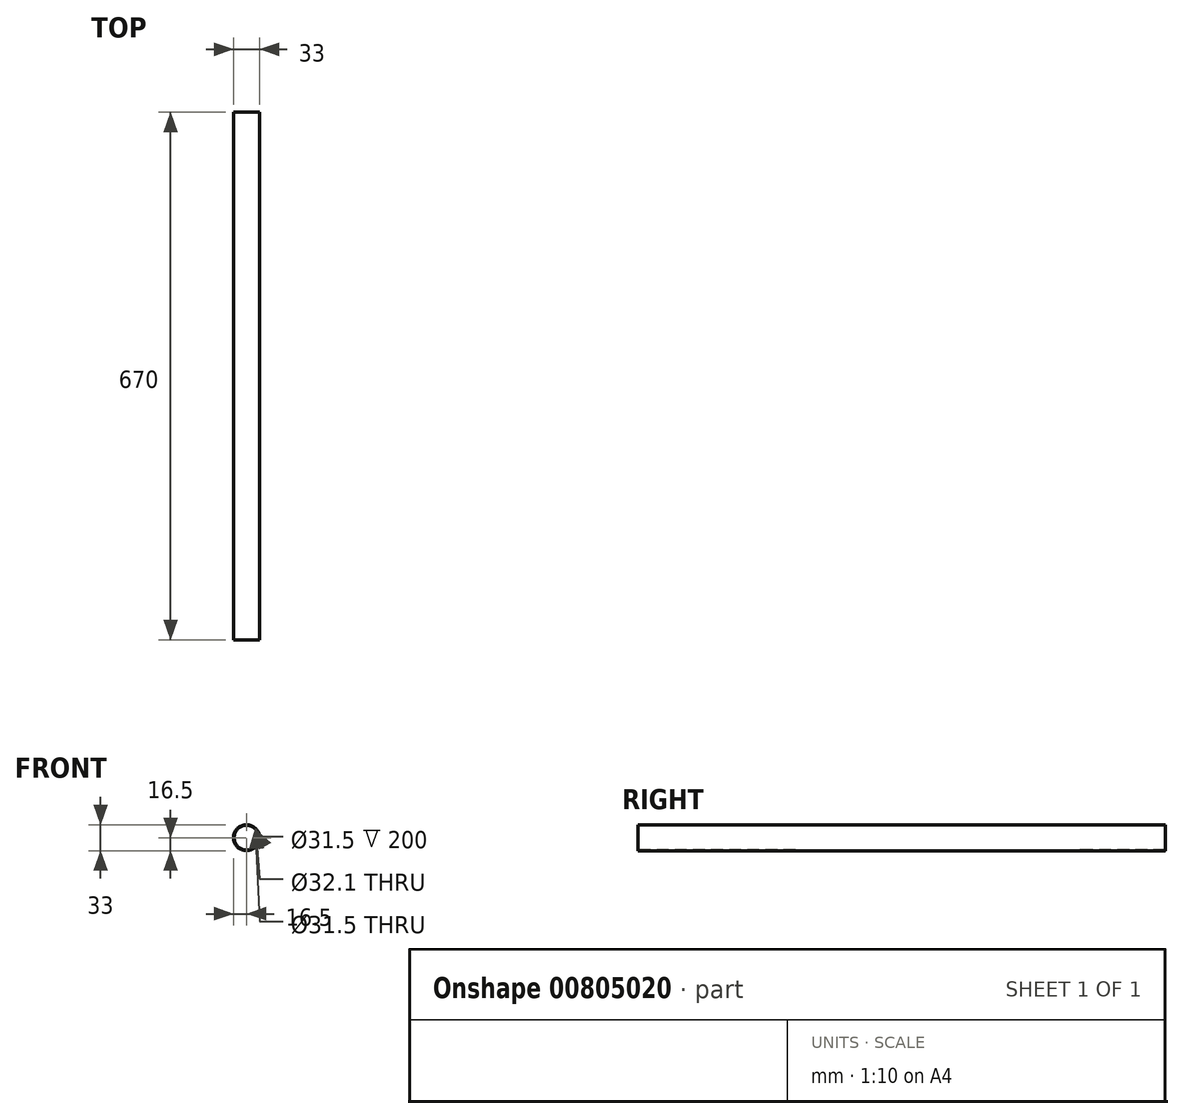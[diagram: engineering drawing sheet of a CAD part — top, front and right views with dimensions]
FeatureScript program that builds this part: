
annotation { "Feature Type Name" : "Feature", "Feature Type Description" : "" }
export const myFeature = defineFeature(function(context is Context, id is Id, definition is map)
    precondition{}
    {
        {
            var Q0;
            Q0=qCreatedBy(makeId("Right.planeOp"),FACE);
            var sketch = newSketch(context, id + "F0", { "sketchPlane" : qUnion([Q0])});
            skLineSegment(sketch, "E0", {"start": v(-335, 16.5) * mm, "end": v(335, 16.5) * mm});
            skLineSegment(sketch, "E1", {"start": v(-335, 0) * mm, "end": v(335, 0) * mm});
            skLineSegment(sketch, "E2", {"start": v(-335, 15.75) * mm, "end": v(-135, 15.75) * mm});
            skLineSegment(sketch, "E3", {"start": v(-135, 15.75) * mm, "end": v(-95, 16.05) * mm});
            skLineSegment(sketch, "E4", {"start": v(-95, 16.05) * mm, "end": v(195, 16.05) * mm});
            skLineSegment(sketch, "E5", {"start": v(195, 16.05) * mm, "end": v(235, 15.75) * mm});
            skLineSegment(sketch, "E6", {"start": v(235, 15.75) * mm, "end": v(335, 15.75) * mm});
            skLineSegment(sketch, "E7", {"start": v(-335, 15.75) * mm, "end": v(-335, 16.5) * mm});
            skLineSegment(sketch, "E8", {"start": v(335, 15.75) * mm, "end": v(335, 16.5) * mm});
            skSolve(sketch);
        }
        {
            var Q0;
            Q0=makeQuery(id+"F0.imprint","IMPRINT",FACE,{"disambiguationData":[TD([[makeQuery(id+"F0.imprint","IMPRINT",EDGE,{"derivedFrom":sQuery(id+"F0.wireOp",EDGE,"E0")}),-1.0]])]});
            var Q1;
            Q1=sQuery(id+"F0.wireOp",EDGE,"E1");
            revolve(context, id + "F1", {"surfaceOperationType" : NewSurfaceOperationType.NEW, "entities" : qUnion([Q0]), "axis" : qUnion([Q1]), "revolveType" : RevolveType.FULL});
        }
    });
